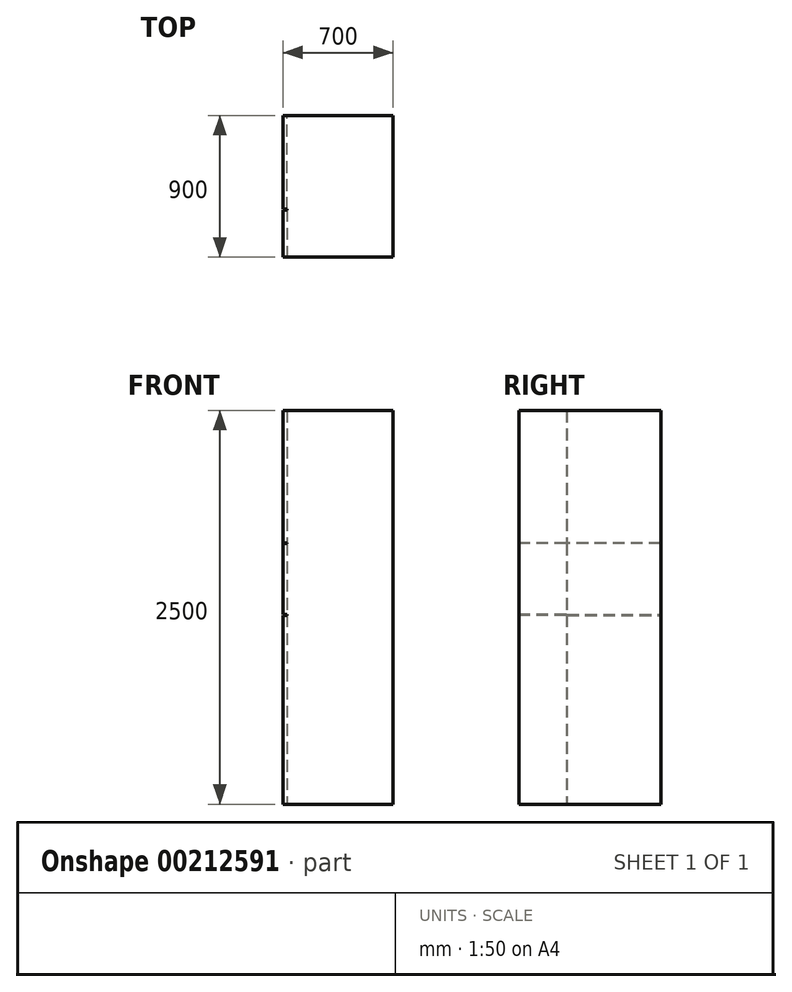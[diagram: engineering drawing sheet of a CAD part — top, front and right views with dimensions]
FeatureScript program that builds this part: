
annotation { "Feature Type Name" : "Feature", "Feature Type Description" : "" }
export const myFeature = defineFeature(function(context is Context, id is Id, definition is map)
    precondition{}
    {
        {
            var Q0;
            Q0=qCreatedBy(makeId("Top.planeOp"),FACE);
            var sketch = newSketch(context, id + "F0", { "sketchPlane" : qUnion([Q0])});
            skLineSegment(sketch, "E0.bottom", {"start": v(0, 0) * mm, "end": v(700, 0) * mm});
            skLineSegment(sketch, "E0.top", {"start": v(0, 900) * mm, "end": v(700, 900) * mm});
            skLineSegment(sketch, "E0.left", {"start": v(0, 0) * mm, "end": v(0, 900) * mm});
            skLineSegment(sketch, "E0.right", {"start": v(700, 0) * mm, "end": v(700, 900) * mm});
            skSolve(sketch);
        }
        {
            var Q0;
            Q0 = qSketchRegion(id + "F0", true);
            extrude(context, id + "F1", {"entities" : qUnion([Q0]), "depth" : 2500 * mm});
        }
        {
            var Q0;
            Q0=qCreatedBy(makeId("Right.planeOp"),FACE);
            var sketch = newSketch(context, id + "F2", { "sketchPlane" : qUnion([Q0])});
            skLineSegment(sketch, "E1.bottom", {"start": v(305, 2500) * mm, "end": v(300, 2500) * mm});
            skLineSegment(sketch, "E1.top", {"start": v(305, 0) * mm, "end": v(300, 0) * mm});
            skLineSegment(sketch, "E1.left", {"start": v(305, 2500) * mm, "end": v(305, 0) * mm});
            skLineSegment(sketch, "E1.right", {"start": v(300, 2500) * mm, "end": v(300, 0) * mm});
            skLineSegment(sketch, "E2.bottom", {"start": v(305, 1205) * mm, "end": v(900, 1205) * mm});
            skLineSegment(sketch, "E2.top", {"start": v(305, 1200) * mm, "end": v(900, 1200) * mm});
            skLineSegment(sketch, "E2.left", {"start": v(305, 1205) * mm, "end": v(305, 1200) * mm});
            skLineSegment(sketch, "E2.right", {"start": v(900, 1205) * mm, "end": v(900, 1200) * mm});
            skLineSegment(sketch, "E3.bottom", {"start": v(300, 1205) * mm, "end": v(0, 1205) * mm});
            skLineSegment(sketch, "E3.top", {"start": v(300, 1200) * mm, "end": v(0, 1200) * mm});
            skLineSegment(sketch, "E3.left", {"start": v(300, 1205) * mm, "end": v(300, 1200) * mm});
            skLineSegment(sketch, "E3.right", {"start": v(0, 1205) * mm, "end": v(0, 1200) * mm});
            skLineSegment(sketch, "E4.bottom", {"start": v(900, 1660) * mm, "end": v(0, 1660) * mm});
            skLineSegment(sketch, "E4.top", {"start": v(900, 1655) * mm, "end": v(0, 1655) * mm});
            skLineSegment(sketch, "E4.left", {"start": v(900, 1660) * mm, "end": v(900, 1655) * mm});
            skLineSegment(sketch, "E4.right", {"start": v(0, 1660) * mm, "end": v(0, 1655) * mm});
            skSolve(sketch);
        }
        {
            var Q0;
            Q0 = qSketchRegion(id + "F2", true);
            extrude(context, id + "F3", {"entities" : qUnion([Q0]), "operationType" : NewBodyOperationType.REMOVE, "depth" : 25 * mm});
        }
    });
